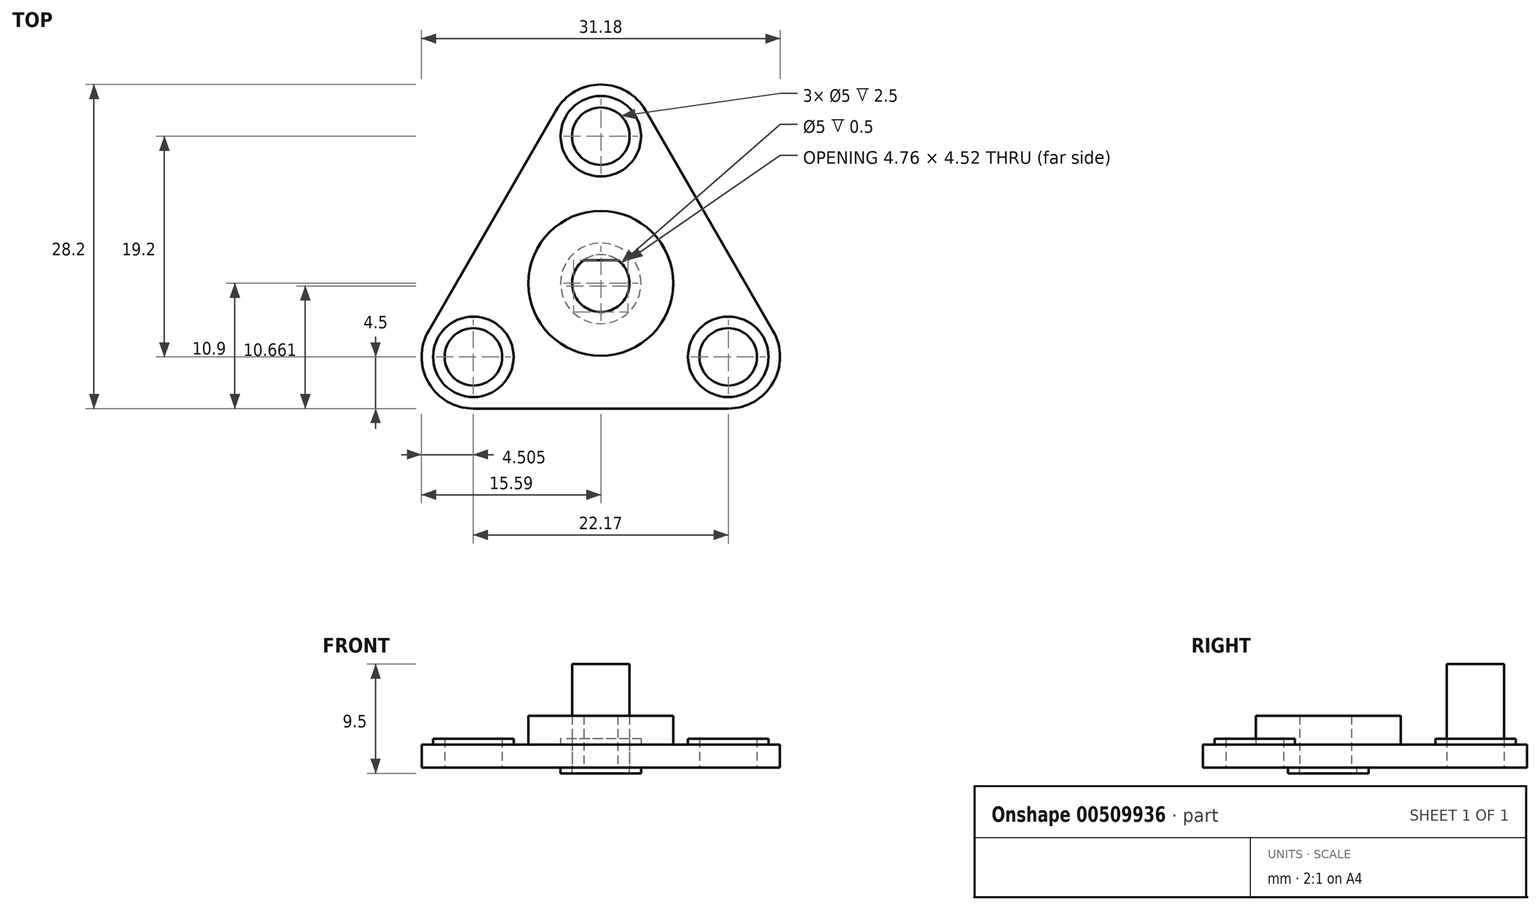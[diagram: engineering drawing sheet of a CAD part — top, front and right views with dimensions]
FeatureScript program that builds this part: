
annotation { "Feature Type Name" : "Feature", "Feature Type Description" : "" }
export const myFeature = defineFeature(function(context is Context, id is Id, definition is map)
    precondition{}
    {
        {
            var Q0;
            Q0=qCreatedBy(makeId("Top.planeOp"),FACE);
            var sketch = newSketch(context, id + "F0", { "sketchPlane" : qUnion([Q0])});
            skCircle(sketch, "E0", {"center": v(0, 0) * mm, "radius": 6.3 * mm});
            skCircle(sketch, "E1", {"center": v(0, 0) * mm, "radius": 17.8 * mm});
            skCircle(sketch, "E2", {"center": v(-11.09, -6.4) * mm, "radius": 4.5 * mm});
            skCircle(sketch, "E3", {"center": v(11.09, -6.4) * mm, "radius": 4.5 * mm});
            skCircle(sketch, "E4", {"center": v(0, 12.8) * mm, "radius": 4.5 * mm});
            skCircle(sketch, "E5", {"center": v(-11.09, -6.4) * mm, "radius": 2.5 * mm});
            skCircle(sketch, "E6", {"center": v(11.09, -6.4) * mm, "radius": 2.5 * mm});
            skCircle(sketch, "E7", {"center": v(0, 12.8) * mm, "radius": 2.5 * mm});
            skLineSegment(sketch, "E8", {"start": v(-11.09, -6.4) * mm, "end": v(0, 12.8) * mm, "construction": true});
            skLineSegment(sketch, "E9", {"start": v(0, 12.8) * mm, "end": v(11.09, -6.4) * mm, "construction": true});
            skLineSegment(sketch, "E10", {"start": v(11.09, -6.4) * mm, "end": v(-11.09, -6.4) * mm, "construction": true});
            skCircle(sketch, "E11", {"center": v(0, 0) * mm, "radius": 2.5 * mm});
            skArc(sketch, "E12.cCircle", {"start": v(-1.47, 2.02) * mm, "mid": v(0, -2.5) * mm, "end": v(1.47, 2.02) * mm, "construction": true});
            skPoint(sketch, "E12.0.midPoint", {"position": v(2.38, -0.77) * mm});
            skArc(sketch, "E13.cCircle", {"start": v(-1.47, 2.02) * mm, "mid": v(0, -2.5) * mm, "end": v(1.47, 2.02) * mm});
            skLineSegment(sketch, "E13.0", {"start": v(2.38, -0.77) * mm, "end": v(2.38, -0.77) * mm});
            skLineSegment(sketch, "E13.1", {"start": v(0, -2.5) * mm, "end": v(0, -2.5) * mm});
            skLineSegment(sketch, "E13.2", {"start": v(-2.38, -0.77) * mm, "end": v(-2.38, -0.77) * mm});
            skLineSegment(sketch, "E13.3", {"start": v(-1.47, 2.02) * mm, "end": v(1.47, 2.02) * mm});
            skLineSegment(sketch, "E13.4", {"start": v(1.47, 2.02) * mm, "end": v(1.47, 2.02) * mm});
            skLineSegment(sketch, "E14.trimOffspring", {"start": v(-1.47, 2.02) * mm, "end": v(-1.47, 2.02) * mm});
            skLineSegment(sketch, "E15", {"start": v(-11.09, -10.9) * mm, "end": v(11.09, -10.9) * mm});
            skLineSegment(sketch, "E16", {"start": v(14.98, -4.15) * mm, "end": v(3.9, 15.05) * mm});
            skLineSegment(sketch, "E17", {"start": v(-3.9, 15.05) * mm, "end": v(-14.98, -4.15) * mm});
            skCircle(sketch, "E18", {"center": v(0, 0) * mm, "radius": 12.8 * mm, "construction": true});
            skSolve(sketch);
        }
        {
            var Q0;
            {var subQ5=sQuery(id+"F0.wireOp",EDGE,"E17");Q0=makeQuery(id+"F0.imprint","IMPRINT",FACE,{"disambiguationData":[TD([[makeQuery(id+"F0.imprint","IMPRINT",EDGE,{"derivedFrom":subQ5}),1.0]])]});}
            var Q1;
            {var subQ4=sQuery(id+"F0.wireOp",EDGE,"E0");var subQ5=makeQuery(id+"F0.imprint","INTERSECT",VERTEX,{"derivedFrom":[subQ4,sQuery(id+"F0.wireOp",EDGE,"E2")]});Q1=makeQuery(id+"F0.imprint","IMPRINT",FACE,{"disambiguationData":[TD([[makeQuery(id+"F0.imprint","IMPRINT",EDGE,{"disambiguationData":[TD([[subQ5,1.0]])],"derivedFrom":subQ4}),1.0]])]});}
            var Q2;
            Q2=makeQuery(id+"F0.imprint","IMPRINT",FACE,{"disambiguationData":[TD([[makeQuery(id+"F0.imprint","IMPRINT",EDGE,{"derivedFrom":sQuery(id+"F0.wireOp",EDGE,"E7")}),-1.0]])]});
            var Q3;
            Q3=makeQuery(id+"F0.imprint","IMPRINT",FACE,{"disambiguationData":[TD([[makeQuery(id+"F0.imprint","IMPRINT",EDGE,{"derivedFrom":sQuery(id+"F0.wireOp",EDGE,"E6")}),-1.0]])]});
            var Q4;
            Q4=makeQuery(id+"F0.imprint","IMPRINT",FACE,{"disambiguationData":[TD([[makeQuery(id+"F0.imprint","IMPRINT",EDGE,{"derivedFrom":sQuery(id+"F0.wireOp",EDGE,"E5")}),-1.0]])]});
            var Q5;
            {var subQ5=sQuery(id+"F0.wireOp",EDGE,"E15");Q5=makeQuery(id+"F0.imprint","IMPRINT",FACE,{"disambiguationData":[TD([[makeQuery(id+"F0.imprint","IMPRINT",EDGE,{"derivedFrom":subQ5}),1.0]])]});}
            var Q6;
            {var subQ5=sQuery(id+"F0.wireOp",EDGE,"E16");Q6=makeQuery(id+"F0.imprint","IMPRINT",FACE,{"disambiguationData":[TD([[makeQuery(id+"F0.imprint","IMPRINT",EDGE,{"derivedFrom":subQ5}),1.0]])]});}
            var Q7;
            {var subQ0=sQuery(id+"F0.wireOp",EDGE,"E13.3");Q7=makeQuery(id+"F0.imprint","IMPRINT",FACE,{"disambiguationData":[TD([[makeQuery(id+"F0.imprint","IMPRINT",EDGE,{"derivedFrom":subQ0}),1.0]])]});}
            extrude(context, id + "F1", {"entities" : qUnion([Q0, Q1, Q2, Q3, Q4, Q5, Q6, Q7]), "depth" : 2 * mm, "offsetDistance" : 25 * mm});
        }
        {
            var Q0;
            Q0=makeQuery(id+"F1.opExtrude","CAP_FACE",FACE,{"disambiguationData":[OSD([sQuery(id+"F0.wireOp",EDGE,"E2"),sQuery(id+"F0.wireOp",EDGE,"E3"),sQuery(id+"F0.wireOp",EDGE,"E4"),sQuery(id+"F0.wireOp",EDGE,"E5"),sQuery(id+"F0.wireOp",EDGE,"E6"),sQuery(id+"F0.wireOp",EDGE,"E7"),sQuery(id+"F0.wireOp",EDGE,"E11"),sQuery(id+"F0.wireOp",EDGE,"E13.3"),sQuery(id+"F0.wireOp",EDGE,"E15"),sQuery(id+"F0.wireOp",EDGE,"E16"),sQuery(id+"F0.wireOp",EDGE,"E17")])],"isStart":false});
            var sketch = newSketch(context, id + "F2", { "sketchPlane" : qUnion([Q0])});
            skCircle(sketch, "E19", {"center": v(0, 0) * mm, "radius": 6.3 * mm});
            skCircle(sketch, "E20", {"center": v(11.09, -6.4) * mm, "radius": 3.5 * mm});
            skCircle(sketch, "E21", {"center": v(0, 12.8) * mm, "radius": 3.5 * mm});
            skCircle(sketch, "E22", {"center": v(-11.09, -6.4) * mm, "radius": 3.5 * mm});
            skSolve(sketch);
        }
        {
            var Q0;
            Q0=makeQuery(id+"F2.imprint","IMPRINT",FACE,{"disambiguationData":[TD([[makeQuery(id+"F2.imprint","IMPRINT",EDGE,{"derivedFrom":sQuery(id+"F2.wireOp",EDGE,"E19")}),1.0]])]});
            extrude(context, id + "F3", {"entities" : qUnion([Q0]), "operationType" : NewBodyOperationType.ADD, "depth" : 2.5 * mm, "offsetDistance" : 25 * mm});
        }
        {
            var Q0;
            Q0=makeQuery(id+"F1.opExtrude","CAP_FACE",FACE,{"disambiguationData":[OSD([sQuery(id+"F0.wireOp",EDGE,"E2"),sQuery(id+"F0.wireOp",EDGE,"E3"),sQuery(id+"F0.wireOp",EDGE,"E4"),sQuery(id+"F0.wireOp",EDGE,"E5"),sQuery(id+"F0.wireOp",EDGE,"E6"),sQuery(id+"F0.wireOp",EDGE,"E7"),sQuery(id+"F0.wireOp",EDGE,"E11"),sQuery(id+"F0.wireOp",EDGE,"E13.3"),sQuery(id+"F0.wireOp",EDGE,"E15"),sQuery(id+"F0.wireOp",EDGE,"E16"),sQuery(id+"F0.wireOp",EDGE,"E17")])],"isStart":true});
            var sketch = newSketch(context, id + "F4", { "sketchPlane" : qUnion([Q0])});
            skCircle(sketch, "E23", {"center": v(0, 0) * mm, "radius": 3.5 * mm});
            skCircle(sketch, "E24", {"center": v(0, 0) * mm, "radius": 2.5 * mm});
            skSolve(sketch);
        }
        {
            var Q0;
            Q0=makeQuery(id+"F4.imprint","IMPRINT",FACE,{"disambiguationData":[TD([[makeQuery(id+"F4.imprint","IMPRINT",EDGE,{"derivedFrom":sQuery(id+"F4.wireOp",EDGE,"E23")}),1.0]])]});
            extrude(context, id + "F5", {"entities" : qUnion([Q0]), "depth" : .5 * mm, "offsetDistance" : 25 * mm});
        }
        {
            var Q0;
            Q0=makeQuery(id+"F2.imprint","IMPRINT",FACE,{"disambiguationData":[TD([[makeQuery(id+"F2.imprint","IMPRINT",EDGE,{"derivedFrom":sQuery(id+"F2.wireOp",EDGE,"E21")}),1.0]])]});
            var Q1;
            Q1=makeQuery(id+"F2.imprint","IMPRINT",FACE,{"disambiguationData":[TD([[makeQuery(id+"F2.imprint","IMPRINT",EDGE,{"derivedFrom":sQuery(id+"F2.wireOp",EDGE,"E22")}),1.0]])]});
            var Q2;
            Q2=makeQuery(id+"F2.imprint","IMPRINT",FACE,{"disambiguationData":[TD([[makeQuery(id+"F2.imprint","IMPRINT",EDGE,{"derivedFrom":sQuery(id+"F2.wireOp",EDGE,"E20")}),1.0]])]});
            extrude(context, id + "F6", {"entities" : qUnion([Q0, Q1, Q2]), "operationType" : NewBodyOperationType.ADD, "depth" : .5 * mm, "offsetDistance" : 25 * mm});
        }
        {
            var Q0;
            Q0=makeQuery(id+"F0.imprint","IMPRINT",FACE,{"disambiguationData":[TD([[makeQuery(id+"F0.imprint","IMPRINT",EDGE,{"derivedFrom":sQuery(id+"F0.wireOp",EDGE,"E7")}),1.0]])]});
            extrude(context, id + "F7", {"entities" : qUnion([Q0]), "depth" : 9 * mm, "offsetDistance" : 25 * mm});
        }
    });
